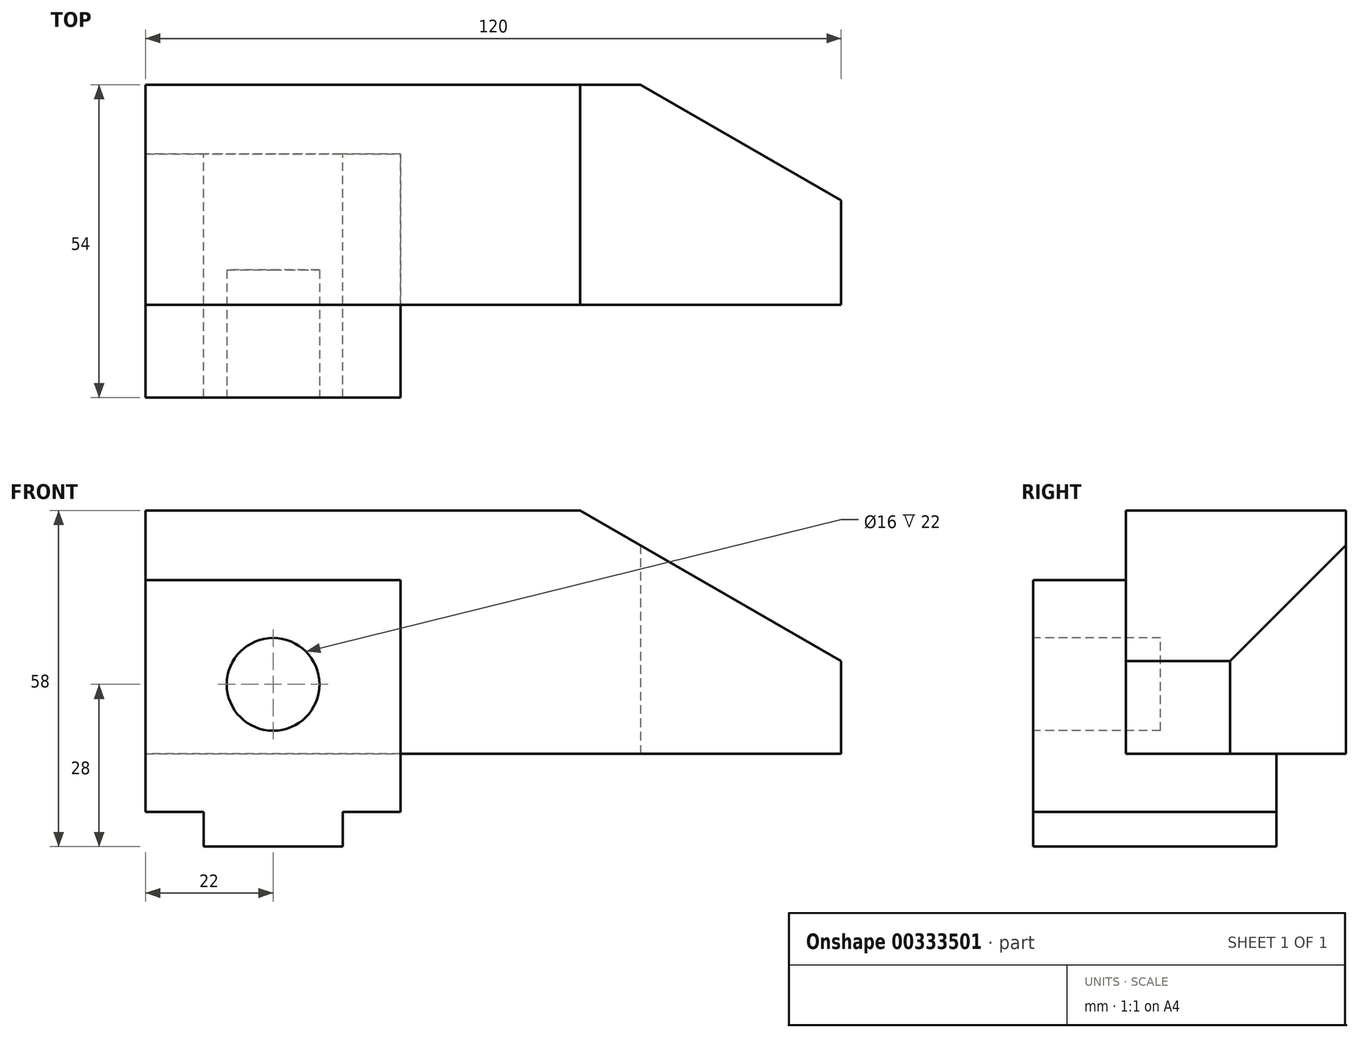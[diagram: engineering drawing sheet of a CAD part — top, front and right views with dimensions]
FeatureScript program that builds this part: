
annotation { "Feature Type Name" : "Feature", "Feature Type Description" : "" }
export const myFeature = defineFeature(function(context is Context, id is Id, definition is map)
    precondition{}
    {
        {
            var Q0;
            Q0=qCreatedBy(makeId("Front.planeOp"),FACE);
            var sketch = newSketch(context, id + "F0", { "sketchPlane" : qUnion([Q0])});
            skLineSegment(sketch, "E0", {"start": v(0, 0) * mm, "end": v(0, 40) * mm});
            skLineSegment(sketch, "E1", {"start": v(0, 40) * mm, "end": v(44, 40) * mm});
            skLineSegment(sketch, "E2", {"start": v(44, 40) * mm, "end": v(44, 0) * mm});
            skLineSegment(sketch, "E3", {"start": v(44, 0) * mm, "end": v(34, 0) * mm});
            skLineSegment(sketch, "E4", {"start": v(34, 0) * mm, "end": v(34, -6) * mm});
            skLineSegment(sketch, "E5", {"start": v(34, -6) * mm, "end": v(10, -6) * mm});
            skLineSegment(sketch, "E6", {"start": v(10, -6) * mm, "end": v(10, 0) * mm});
            skLineSegment(sketch, "E7", {"start": v(10, 0) * mm, "end": v(0, 0) * mm});
            skSolve(sketch);
        }
        {
            var Q0;
            Q0=makeQuery(id+"F0.imprint","IMPRINT",FACE,{"disambiguationData":[TD([[makeQuery(id+"F0.imprint","IMPRINT",EDGE,{"derivedFrom":sQuery(id+"F0.wireOp",EDGE,"E0")}),-1.0]])]});
            extrude(context, id + "F1", {"entities" : qUnion([Q0]), "depth" : 16 * mm});
        }
        {
            var Q0;
            Q0=makeQuery(id+"F0.imprint","IMPRINT",FACE,{"disambiguationData":[TD([[makeQuery(id+"F0.imprint","IMPRINT",EDGE,{"derivedFrom":sQuery(id+"F0.wireOp",EDGE,"E0")}),-1.0]])]});
            var sketch = newSketch(context, id + "F2", { "sketchPlane" : qUnion([Q0])});
            skLineSegment(sketch, "E8", {"start": v(0, 10) * mm, "end": v(0, 52) * mm});
            skLineSegment(sketch, "E9", {"start": v(0, 52) * mm, "end": v(75, 52) * mm});
            skLineSegment(sketch, "E10", {"start": v(75, 52) * mm, "end": v(120, 26.02) * mm});
            skLineSegment(sketch, "E11", {"start": v(120, 26.02) * mm, "end": v(120, 10) * mm});
            skLineSegment(sketch, "E12", {"start": v(120, 10) * mm, "end": v(0, 10) * mm});
            skLineSegment(sketch, "E13", {"start": v(75, 52) * mm, "end": v(180.52, 52) * mm, "construction": true});
            skSolve(sketch);
        }
        {
            var Q0;
            {var subQ5=sQuery(id+"F2.wireOp",EDGE,"E9");Q0=makeQuery(id+"F2.imprint","IMPRINT",FACE,{"disambiguationData":[TD([[makeQuery(id+"F2.imprint","IMPRINT",EDGE,{"derivedFrom":subQ5}),-1.0]])]});}
            var Q1;
            {var subQ1=makeQuery(id+"F0.imprint","IMPRINT",EDGE,{"derivedFrom":sQuery(id+"F0.wireOp",EDGE,"E1")});Q1=makeQuery(id+"F2.imprint","IMPRINT",FACE,{"disambiguationData":[TD([[makeQuery(id+"F2.imprint","IMPRINT",EDGE,{"derivedFrom":subQ1}),-1.0]])]});}
            extrude(context, id + "F3", {"entities" : qUnion([Q0, Q1]), "operationType" : NewBodyOperationType.ADD, "oppositeDirection" : true, "depth" : 18 * mm});
        }
        {
            var Q0;
            Q0=makeQuery(id+"F1.opExtrude","CAP_FACE",FACE,{"disambiguationData":[OSD([sQuery(id+"F0.wireOp",EDGE,"E0"),sQuery(id+"F0.wireOp",EDGE,"E1"),sQuery(id+"F0.wireOp",EDGE,"E2"),sQuery(id+"F0.wireOp",EDGE,"E3"),sQuery(id+"F0.wireOp",EDGE,"E4"),sQuery(id+"F0.wireOp",EDGE,"E5"),sQuery(id+"F0.wireOp",EDGE,"E6"),sQuery(id+"F0.wireOp",EDGE,"E7")])],"isStart":false});
            var sketch = newSketch(context, id + "F4", { "sketchPlane" : qUnion([Q0])});
            skCircle(sketch, "E14", {"center": v(22, 22) * mm, "radius": 8 * mm});
            skSolve(sketch);
        }
        {
            var Q0;
            Q0=makeQuery(id+"F4.imprint","IMPRINT",FACE,{"disambiguationData":[TD([[makeQuery(id+"F4.imprint","IMPRINT",EDGE,{"derivedFrom":sQuery(id+"F4.wireOp",EDGE,"E14")}),1.0]])]});
            extrude(context, id + "F5", {"entities" : qUnion([Q0]), "operationType" : NewBodyOperationType.REMOVE, "oppositeDirection" : true, "depth" : 22 * mm});
        }
        {
            var Q0;
            Q0=makeQuery(id+"F0.imprint","IMPRINT",FACE,{"disambiguationData":[TD([[makeQuery(id+"F0.imprint","IMPRINT",EDGE,{"derivedFrom":sQuery(id+"F0.wireOp",EDGE,"E0")}),-1.0]])]});
            var sketch = newSketch(context, id + "F6", { "sketchPlane" : qUnion([Q0])});
            skLineSegment(sketch, "E15", {"start": v(0, 10) * mm, "end": v(44, 10) * mm});
            skLineSegment(sketch, "E16", {"start": v(44, 10) * mm, "end": v(44, 0) * mm});
            skLineSegment(sketch, "E17", {"start": v(44, 0) * mm, "end": v(34, 0) * mm});
            skLineSegment(sketch, "E18", {"start": v(34, 0) * mm, "end": v(34, -6) * mm});
            skLineSegment(sketch, "E19", {"start": v(34, -6) * mm, "end": v(10, -6) * mm});
            skLineSegment(sketch, "E20", {"start": v(10, -6) * mm, "end": v(10, 0) * mm});
            skLineSegment(sketch, "E21", {"start": v(10, 0) * mm, "end": v(0, 0) * mm});
            skLineSegment(sketch, "E22", {"start": v(0, 0) * mm, "end": v(0, 10) * mm});
            skSolve(sketch);
        }
        {
            var Q0;
            Q0=makeQuery(id+"F6.imprint","IMPRINT",FACE,{"disambiguationData":[TD([[makeQuery(id+"F6.imprint","IMPRINT",EDGE,{"derivedFrom":sQuery(id+"F6.wireOp",EDGE,"E15")}),-1.0]])]});
            extrude(context, id + "F7", {"entities" : qUnion([Q0]), "operationType" : NewBodyOperationType.ADD, "oppositeDirection" : true, "depth" : 26 * mm});
        }
        {
            var Q0;
            Q0=makeQuery(id+"F3.opExtrude","SWEPT_FACE",FACE,{"disambiguationData":[OSD([sQuery(id+"F2.wireOp",EDGE,"E12")])]});
            var sketch = newSketch(context, id + "F8", { "sketchPlane" : qUnion([Q0])});
            skLineSegment(sketch, "E23", {"start": v(85.36, -38) * mm, "end": v(120, -18) * mm});
            skLineSegment(sketch, "E24", {"start": v(85.36, -38) * mm, "end": v(85.36, -18) * mm});
            skLineSegment(sketch, "E25", {"start": v(85.36, -18) * mm, "end": v(120, -18) * mm});
            skLineSegment(sketch, "E26", {"start": v(85.36, -38) * mm, "end": v(143.77, -38) * mm, "construction": true});
            skSolve(sketch);
        }
        {
            var Q0;
            Q0=makeQuery(id+"F8.imprint","IMPRINT",FACE,{"disambiguationData":[TD([[makeQuery(id+"F8.imprint","IMPRINT",EDGE,{"derivedFrom":sQuery(id+"F8.wireOp",EDGE,"E23")}),1.0]])]});
            extrude(context, id + "F9", {"entities" : qUnion([Q0]), "operationType" : NewBodyOperationType.ADD, "oppositeDirection" : true, "depth" : 42 * mm});
        }
        {
            var Q0;
            Q0=makeQuery(id+"F9.opExtrude","SWEPT_FACE",FACE,{"disambiguationData":[OSD([sQuery(id+"F8.wireOp",EDGE,"E25")])]});
            var sketch = newSketch(context, id + "F10", { "sketchPlane" : qUnion([Q0])});
            skLineSegment(sketch, "E27", {"start": v(85.36, 52) * mm, "end": v(120, 52) * mm});
            skLineSegment(sketch, "E28", {"start": v(120, 52) * mm, "end": v(120, 26.02) * mm});
            skLineSegment(sketch, "E29", {"start": v(120, 26.02) * mm, "end": v(85.36, 46.02) * mm});
            skLineSegment(sketch, "E30", {"start": v(85.36, 46.02) * mm, "end": v(85.36, 52) * mm});
            skSolve(sketch);
        }
        {
            var Q0;
            Q0=makeQuery(id+"F10.imprint","IMPRINT",FACE,{"disambiguationData":[TD([[makeQuery(id+"F10.imprint","IMPRINT",EDGE,{"derivedFrom":sQuery(id+"F10.wireOp",EDGE,"E27")}),1.0]])]});
            extrude(context, id + "F11", {"entities" : qUnion([Q0]), "operationType" : NewBodyOperationType.REMOVE, "endBound" : BoundingType.THROUGH_ALL, "oppositeDirection" : true, "depth" : 25 * mm});
        }
        {
            var Q0;
            Q0=makeQuery(id+"F3.opExtrude","CAP_FACE",FACE,{"disambiguationData":[OSD([sQuery(id+"F2.wireOp",EDGE,"E8"),sQuery(id+"F2.wireOp",EDGE,"E9"),sQuery(id+"F2.wireOp",EDGE,"E10"),sQuery(id+"F2.wireOp",EDGE,"E11"),sQuery(id+"F2.wireOp",EDGE,"E12")])],"isStart":false});
            var sketch = newSketch(context, id + "F12", { "sketchPlane" : qUnion([Q0])});
            skLineSegment(sketch, "E31", {"start": v(-85.36, 46.02) * mm, "end": v(-75, 52) * mm});
            skLineSegment(sketch, "E32", {"start": v(-75, 52) * mm, "end": v(0, 52) * mm});
            skLineSegment(sketch, "E33", {"start": v(0, 52) * mm, "end": v(0, 10) * mm});
            skLineSegment(sketch, "E34", {"start": v(0, 10) * mm, "end": v(-85.36, 10) * mm});
            skLineSegment(sketch, "E35", {"start": v(-85.36, 10) * mm, "end": v(-85.36, 46.02) * mm});
            skSolve(sketch);
        }
        {
            var Q0;
            Q0=makeQuery(id+"F12.imprint","IMPRINT",FACE,{"disambiguationData":[TD([[makeQuery(id+"F12.imprint","IMPRINT",EDGE,{"derivedFrom":sQuery(id+"F12.wireOp",EDGE,"E31")}),1.0]])]});
            extrude(context, id + "F13", {"entities" : qUnion([Q0]), "operationType" : NewBodyOperationType.ADD, "depth" : 20 * mm});
        }
    });
